# Revit family: BE_88301_de_DE
name_source: partatom
category: Leuchten
units: mm (PartAtom-declared; Revit-internal decimal feet)

## family parameters
Basisbauteil = Fläche
Beim Laden mit Abzugskörper schneiden = Ja
Bemaßung runder Anschluss = Durchmesser verwenden
Gemeinsam genutzt = Nein
Lichtquelle = Ja
Raumberechnungspunkt = Ja
Teiletyp = Normal

## types (3) — shared parameters
AC/DC = DC
Aktualisierung = 2022-05-19T04:00:07
BEGA_Dummy = Nein
BEGA_IES = Ja
BEGA_Intern = Ja
BEGA_Intern_Konstruktion = Ja
BEGA_Intern_an = Ja
BEGA_Intern_aus = Ja
Beschreibung = Bodeneinbauleuchte
Beschreibung_Sonderanfertigung = Hier können Sie Informationen zur Sonderanfertigung eintragen.
CE_Konformität = ja
Einbau_in_Wärmedämmung = ungeeignet
Energieeffizienzklasse = LED A++ - A
Farbfilter = 16777215
Farbtemperaturverschiebung bei Dämpfen der Lampe = <Keine Auswahl>
Farbwiedergabeindex = CRI > 80
Gewicht = 0.9 kg
Hersteller = BEGA
Lampe = LED 0.2 W
Lastklassifizierung = Beleuchtung
Lebensdauerkriterien = L70B50 @ 25 °C = 200000 h
Logo = BEGA_Logo.png
Material_06 = BEGA_Oberfläche_Edelstahl_gebürstet
Material_11 = BEGA_Glas_opal
Material_15 = BEGA_Leuchtmedium_matt
Material_17 = BEGA_Reflektor
Neigungswinkel = 0.00°
Produktdatenblatt = https://cdn.bega.com
Schutzart = IP 67
Schutzklasse = III
Sonderanfertigung = Nein
Spannung = 24 V
Typenbild = 88301.png
URL = https://www.bega.com
zero-valued in all types: Vorgabe-Ansicht

## per-type parameters (varying)
| type | Bestellnummer | Datei für fotometrisches Netz | Farbtemperatur | LED_Modulbezeichnung | Lampenlichtstrom | Modell |
| BEGA_88301_K4 | 88301K4 | BE_88301K4.IES | 4000 K | LED-0157/840 | 40 lm | 88301K4 |
| BEGA_88301_K3 | 88301K3 | BE_88301K3.IES | 3000 K | LED-0157/830 | 40 lm | 88301K3 |
| BEGA_88301_K27 | 88301K27 | BE_88301K27.IES | 2700 K | LED-0157/827 | 35 lm | 88301K27 |
